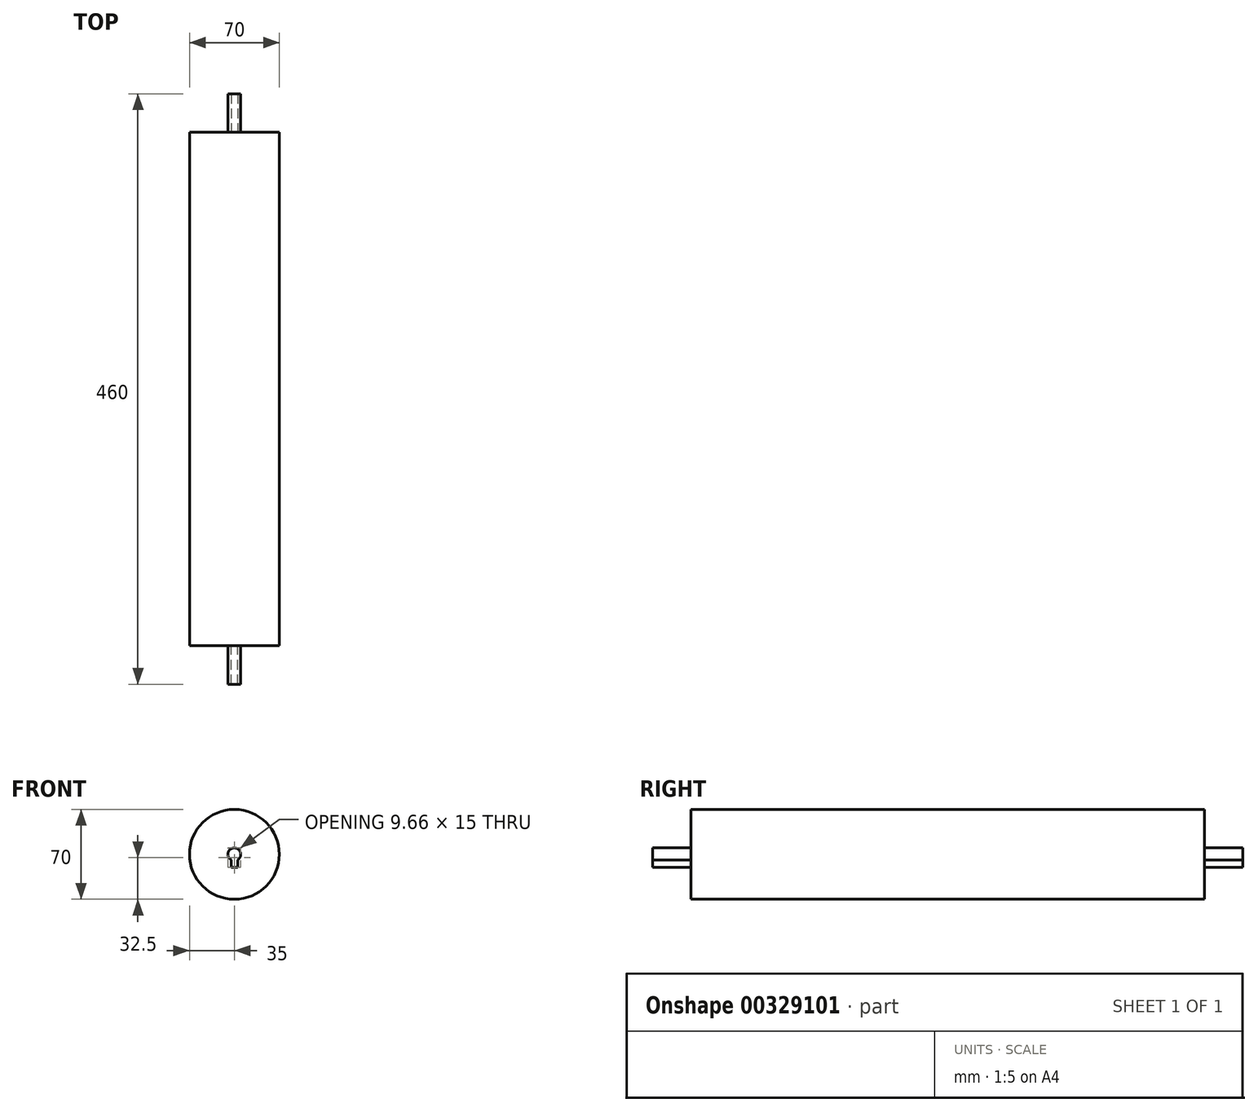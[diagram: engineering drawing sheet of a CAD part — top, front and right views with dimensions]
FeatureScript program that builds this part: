
annotation { "Feature Type Name" : "Feature", "Feature Type Description" : "" }
export const myFeature = defineFeature(function(context is Context, id is Id, definition is map)
    precondition{}
    {
        {
            var Q0;
            Q0=qCreatedBy(makeId("Front.planeOp"),FACE);
            var sketch = newSketch(context, id + "F0", { "sketchPlane" : qUnion([Q0])});
            skCircle(sketch, "E0", {"center": v(0, 0) * mm, "radius": 35 * mm});
            skSolve(sketch);
        }
        {
            var Q0;
            Q0 = qSketchRegion(id + "F0", true);
            extrude(context, id + "F1", {"entities" : qUnion([Q0]), "depth" : 400 * mm});
        }
        {
            var Q0;
            Q0=qCreatedBy(makeId("Front.planeOp"),FACE);
            var sketch = newSketch(context, id + "F2", { "sketchPlane" : qUnion([Q0])});
            skCircle(sketch, "E1", {"center": v(0, 0) * mm, "radius": 5 * mm});
            skSolve(sketch);
        }
        {
            var Q0;
            Q0 = qSketchRegion(id + "F2", true);
            extrude(context, id + "F3", {"entities" : qUnion([Q0]), "operationType" : NewBodyOperationType.ADD, "oppositeDirection" : true, "depth" : 30 * mm});
        }
        {
            var Q0;
            Q0 = qSketchRegion(id + "F2", true);
            extrude(context, id + "F4", {"entities" : qUnion([Q0]), "operationType" : NewBodyOperationType.ADD, "depth" : 430 * mm});
        }
        {
            var Q0;
            Q0=makeQuery(id+"F1.opExtrude","CAP_FACE",FACE,{"disambiguationData":[OSD([sQuery(id+"F0.wireOp",EDGE,"E0")])],"isStart":false});
            var sketch = newSketch(context, id + "F5", { "sketchPlane" : qUnion([Q0])});
            skLineSegment(sketch, "E2", {"start": v(-2.5, -4.33) * mm, "end": v(-2.5, -10) * mm});
            skLineSegment(sketch, "E3", {"start": v(-2.5, -10) * mm, "end": v(2.5, -10) * mm});
            skLineSegment(sketch, "E4", {"start": v(2.5, -10) * mm, "end": v(2.5, -4.33) * mm});
            skLineSegment(sketch, "E5", {"start": v(0, 0) * mm, "end": v(0, -10) * mm, "construction": true});
            skSolve(sketch);
        }
        {
            var Q0;
            {var subQ0=sQuery(id+"F5.wireOp",EDGE,"E2");Q0=makeQuery(id+"F5.imprint","IMPRINT",FACE,{"disambiguationData":[TD([[makeQuery(id+"F5.imprint","IMPRINT",EDGE,{"derivedFrom":subQ0}),1.0]])]});}
            extrude(context, id + "F6", {"entities" : qUnion([Q0]), "operationType" : NewBodyOperationType.ADD, "depth" : 60 * mm, "symmetric" : true});
        }
        {
            var Q0;
            {var subQ0=sQuery(id+"F5.wireOp",EDGE,"E2");Q0=makeQuery(id+"F5.imprint","IMPRINT",FACE,{"disambiguationData":[TD([[makeQuery(id+"F5.imprint","IMPRINT",EDGE,{"derivedFrom":subQ0}),1.0]])]});}
            extrude(context, id + "F7", {"entities" : qUnion([Q0]), "operationType" : NewBodyOperationType.ADD, "oppositeDirection" : true, "depth" : 430 * mm});
        }
    });
